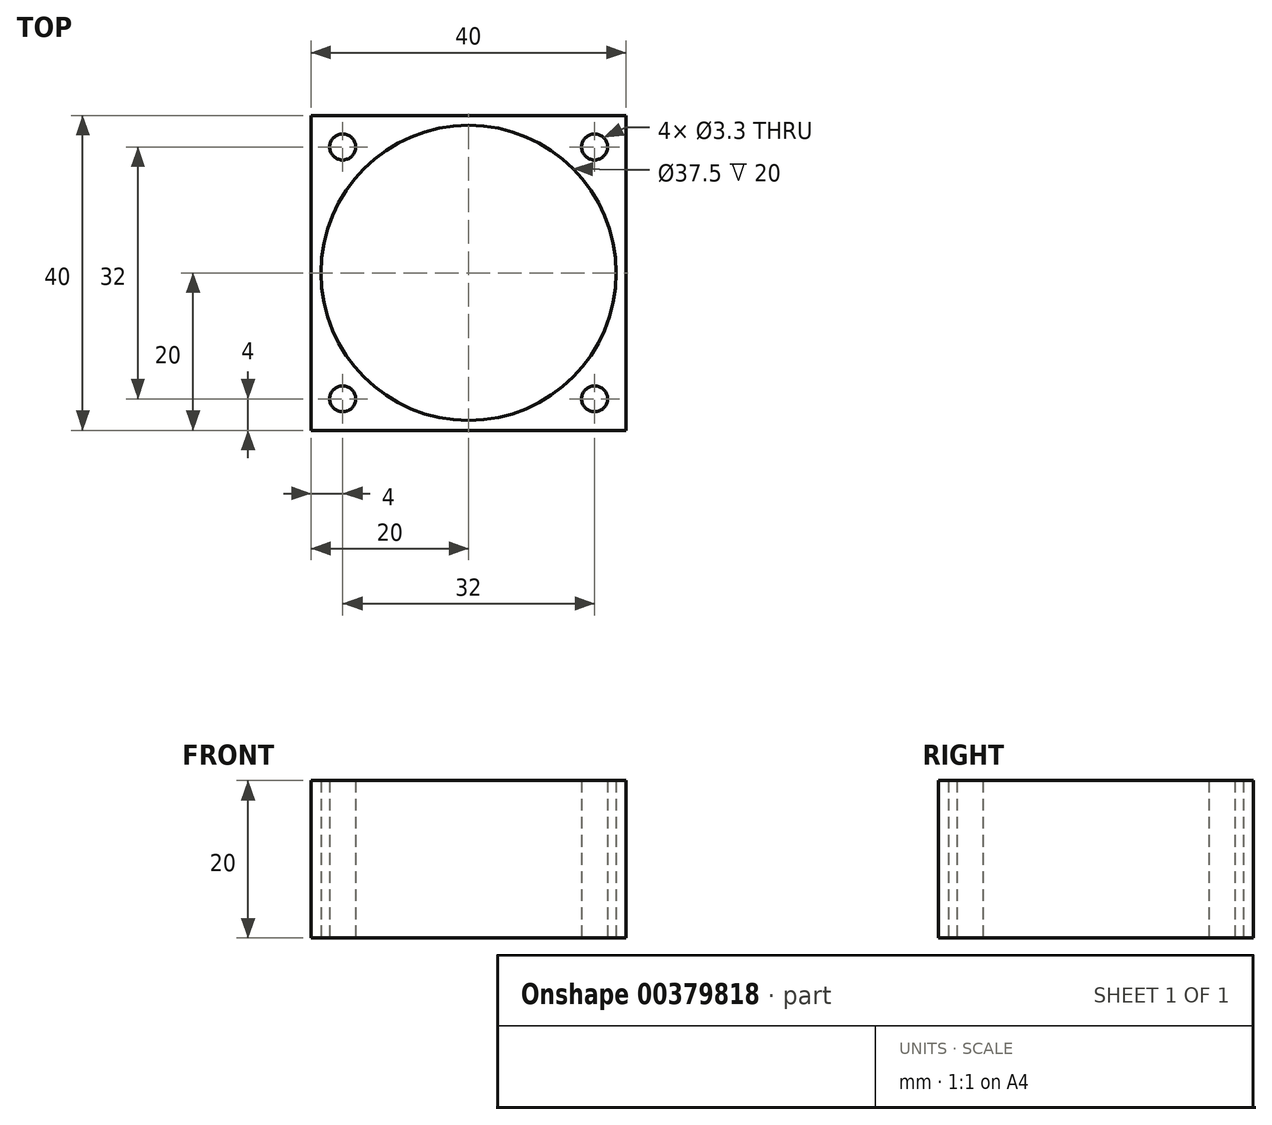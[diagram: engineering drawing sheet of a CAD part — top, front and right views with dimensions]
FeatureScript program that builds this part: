
annotation { "Feature Type Name" : "Feature", "Feature Type Description" : "" }
export const myFeature = defineFeature(function(context is Context, id is Id, definition is map)
    precondition{}
    {
        {
            var Q0;
            Q0=qCreatedBy(makeId("Top.planeOp"),FACE);
            var sketch = newSketch(context, id + "F0", { "sketchPlane" : qUnion([Q0])});
            skLineSegment(sketch, "E0.bottom", {"start": v(0, 0) * mm, "end": v(40, 0) * mm});
            skLineSegment(sketch, "E0.top", {"start": v(0, 40) * mm, "end": v(40, 40) * mm});
            skLineSegment(sketch, "E0.left", {"start": v(0, 0) * mm, "end": v(0, 40) * mm});
            skLineSegment(sketch, "E0.right", {"start": v(40, 0) * mm, "end": v(40, 40) * mm});
            skCircle(sketch, "E1", {"center": v(20, 20) * mm, "radius": 18.75 * mm});
            skPoint(sketch, "E1.centerSnap0", {"position": v(40, 20) * mm});
            skPoint(sketch, "E1.centerSnap1", {"position": v(20, 40) * mm});
            skCircle(sketch, "E2", {"center": v(4, 36) * mm, "radius": 1.65 * mm});
            skCircle(sketch, "E3", {"center": v(4, 4) * mm, "radius": 1.65 * mm});
            skCircle(sketch, "E4", {"center": v(36, 4) * mm, "radius": 1.65 * mm});
            skCircle(sketch, "E5", {"center": v(36, 36) * mm, "radius": 1.65 * mm});
            skSolve(sketch);
        }
        {
            var Q0;
            Q0 = qSketchRegion(id + "F0", true);
            extrude(context, id + "F1", {"entities" : qUnion([Q0]), "depth" : 20 * mm});
        }
    });
